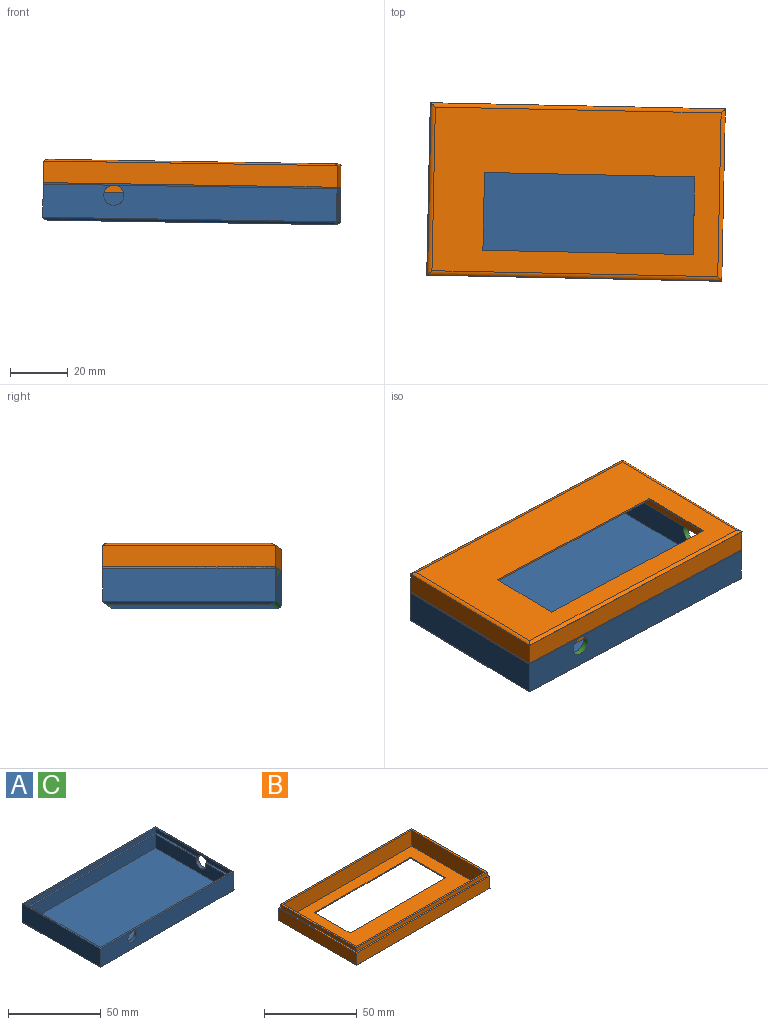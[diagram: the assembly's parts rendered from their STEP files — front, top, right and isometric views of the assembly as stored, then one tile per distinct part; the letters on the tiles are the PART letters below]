
ASSEMBLY  parts=3 mates=1
PART A: 25 faces, bbox 102.1x59.8x13 mm
  f0: plane 100.1x57.55mm, normal (0,0,1), area 194mm2, adj f9,f10,f11,f12,f15,f16,f17,f18
  f1: plane 102x59.8mm, normal (0,0,-1), area 15.9mm2, adj f2,f3,f4,f5,f21,f22,f24
  f2: plane 59.8x12mm, normal (-1,0,0), area 717.6mm2, adj f1,f3,f5,f6
  f3: plane 102x12mm, normal (0,-1,0), area 1185.5mm2, adj f1,f2,f4,f6,f20
  f4: plane 59.8x12mm, normal (1,0,0), area 673.4mm2, adj f1,f3,f5,f6,f7,f19
  f5: plane 102x12mm, normal (0,1,0), area 1224mm2, adj f1,f2,f4,f6
  f6: plane 102x59.8mm, normal (0,0,1), area 338.7mm2, adj f2,f3,f4,f5,f9,f10,f11,f12
  f7: plane 59.67x0.1mm, normal (0,0,1), area 5.8mm2, adj f4,f21,f23,f24
  f8: plane 98.6x56.2mm, normal (0,0,-1), area 5541.3mm2, adj f21,f22,f23,f24
  f9: plane 57.55x3mm, normal (1,0,0), area 172.7mm2, adj f0,f6,f10,f12
  f10: plane 100.1x3mm, normal (0,1,0), area 288mm2, adj f0,f6,f9,f11,f13,f20
  f11: plane 57.55x3mm, normal (-1,0,0), area 161.5mm2, adj f0,f6,f10,f12,f13,f19
  f12: plane 100.1x3mm, normal (0,-1,0), area 300.3mm2, adj f0,f6,f9,f11
  f13: plane 73.28x18.62mm, normal (0,0,1), area 84.8mm2, adj f10,f11,f15,f18,f19,f20
  f14: plane 98x55.8mm, normal (0,0,1), area 5468.4mm2, adj f15,f16,f17,f18
  f15: plane 55.8x9mm, normal (-1,0,0), area 469.2mm2, adj f0,f13,f14,f16,f18,f19
  f16: plane 98x9mm, normal (0,-1,0), area 882mm2, adj f0,f14,f15,f17
  f17: plane 55.8x9mm, normal (1,0,0), area 502.2mm2, adj f0,f14,f16,f18
  f18: plane 98x9mm, normal (0,1,0), area 855.9mm2, adj f0,f13,f14,f15,f17,f20
  f19: cylinder r=3.75mm len=7.5mm, axis (1,0,0), area 37.3mm2, adj f0,f4,f11,f13,f15
  f20: cylinder r=3.5mm len=7mm, axis (0,-1,0), area 36.1mm2, adj f0,f3,f10,f13,f18
  f21: cylinder r=2mm len=102.06mm, axis (-1,0,0), area 210.5mm2, adj f1,f7,f8,f22,f23
  f22: cylinder r=2mm len=59.67mm, axis (0,-1,0), area 121.7mm2, adj f1,f8,f21,f24
  f23: cylinder r=2mm len=59.67mm, axis (0,-1,0), area 121.7mm2, adj f7,f8,f21,f24
  f24: cylinder r=2mm len=102.06mm, axis (-1,0,0), area 210.5mm2, adj f1,f7,f8,f22,f23
PART B: 26 faces, bbox 102.1x59.8x11.1 mm
  f0: plane 102x59.8mm, normal (0,0,-1), area 15.9mm2, adj f1,f2,f3,f4,f18,f19,f21
  f1: plane 59.8x8mm, normal (-1,0,0), area 478.4mm2, adj f0,f2,f4,f5
  f2: plane 102x8mm, normal (0,-1,0), area 816mm2, adj f0,f1,f3,f5
  f3: plane 59.8x8mm, normal (1,0,0), area 478.4mm2, adj f0,f2,f4,f5,f6
  f4: plane 102x8mm, normal (0,1,0), area 816mm2, adj f0,f1,f3,f5
  f5: plane 102x59.8mm, normal (0,0,1), area 338.7mm2, adj f1,f2,f3,f4,f8,f9,f10,f11
  f6: plane 59.67x0.1mm, normal (0,0,1), area 5.8mm2, adj f3,f18,f20,f21
  f7: plane 99.21x56.81mm, normal (0,0,-1), area 3664.7mm2, adj f18,f19,f20,f21,f22,f23,f24,f25
  f8: plane 57.55x2.5mm, normal (-1,0,0), area 143.9mm2, adj f5,f9,f11,f12
  f9: plane 100.1x2.5mm, normal (0,-1,0), area 250.3mm2, adj f5,f8,f10,f12
  f10: plane 57.55x2.5mm, normal (1,0,0), area 143.9mm2, adj f5,f9,f11,f12
  f11: plane 100.1x2.5mm, normal (0,1,0), area 250.3mm2, adj f5,f8,f10,f12
  f12: plane 100.1x57.55mm, normal (0,0,1), area 292.5mm2, adj f8,f9,f10,f11,f14,f15,f16,f17
  f13: plane 98x55.8mm, normal (0,0,1), area 3497.4mm2, adj f14,f15,f16,f17,f22,f23,f24,f25
  f14: plane 55.8x10.5mm, normal (-1,0,0), area 585.9mm2, adj f12,f13,f15,f17
  f15: plane 98x10.5mm, normal (0,-1,0), area 1029mm2, adj f12,f13,f14,f16
  f16: plane 55.8x10.5mm, normal (1,0,0), area 585.9mm2, adj f12,f13,f15,f17
  f17: plane 98x10.5mm, normal (0,1,0), area 1029mm2, adj f12,f13,f14,f16
  f18: cylinder r=2mm len=102.06mm, axis (-1,0,0), area 160.2mm2, adj f0,f6,f7,f19,f20
  f19: cylinder r=2mm len=59.67mm, axis (0,-1,0), area 92.8mm2, adj f0,f7,f18,f21
  f20: cylinder r=2mm len=59.67mm, axis (0,-1,0), area 92.8mm2, adj f6,f7,f18,f21
  f21: cylinder r=2mm len=102.06mm, axis (-1,0,0), area 160.2mm2, adj f0,f6,f7,f19,f20
  f22: plane 27x0.6mm, normal (1,0,0), area 16.2mm2, adj f7,f13,f23,f25
  f23: plane 73x0.6mm, normal (0,1,0), area 43.8mm2, adj f7,f13,f22,f24
  f24: plane 27x0.6mm, normal (-1,0,0), area 16.2mm2, adj f7,f13,f23,f25
  f25: plane 73x0.6mm, normal (0,-1,0), area 43.8mm2, adj f7,f13,f22,f24
PART C: same geometry as A
PLACE A rot(axis=(0,0.61,-0.8),1.5deg) t=(-32.16,-39.96,-31.49)mm
PLACE B rot(axis=(1,-0.01,-0.01),180deg) t=(-31.9,-42.66,-12)mm
PLACE C rot(axis=(0,0.61,-0.8),1.5deg) t=(-32.16,-39.96,-31.49)mm
MATE slider B.f12 <-> C.f0  axis (-0.02,0,-1) through (-91.61,-12.17,-21.55)mm
